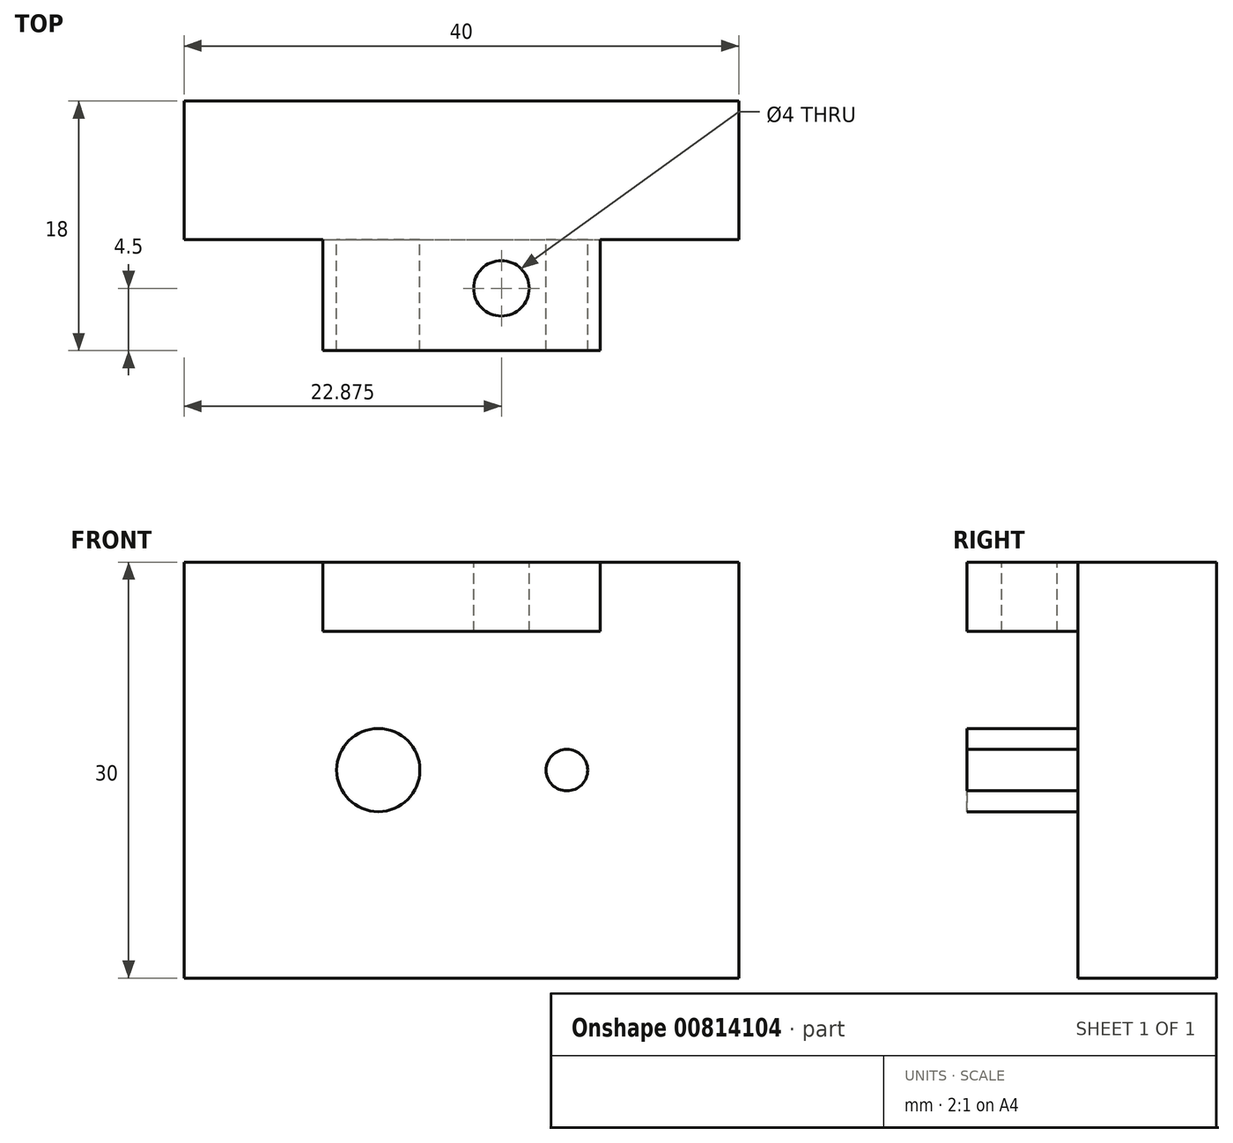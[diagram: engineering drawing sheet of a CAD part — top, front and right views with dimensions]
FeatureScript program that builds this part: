
annotation { "Feature Type Name" : "Feature", "Feature Type Description" : "" }
export const myFeature = defineFeature(function(context is Context, id is Id, definition is map)
    precondition{}
    {
        {
            var Q0;
            Q0=qCreatedBy(makeId("Front.planeOp"),FACE);
            var sketch = newSketch(context, id + "F0", { "sketchPlane" : qUnion([Q0])});
            skLineSegment(sketch, "E0.bottom", {"start": v(0, 0) * mm, "end": v(40, 0) * mm});
            skLineSegment(sketch, "E0.top", {"start": v(0, 30) * mm, "end": v(40, 30) * mm});
            skLineSegment(sketch, "E0.left", {"start": v(0, 0) * mm, "end": v(0, 30) * mm});
            skLineSegment(sketch, "E0.right", {"start": v(40, 0) * mm, "end": v(40, 30) * mm});
            skSolve(sketch);
        }
        {
            var Q0;
            Q0 = qSketchRegion(id + "F0", true);
            extrude(context, id + "F1", {"entities" : qUnion([Q0]), "depth" : 10 * mm, "offsetDistance" : 25 * mm});
        }
        {
            var Q0;
            Q0=makeQuery(id+"F1.opExtrude","CAP_FACE",FACE,{"disambiguationData":[OSD([sQuery(id+"F0.wireOp",EDGE,"E0.bottom"),sQuery(id+"F0.wireOp",EDGE,"E0.top"),sQuery(id+"F0.wireOp",EDGE,"E0.left"),sQuery(id+"F0.wireOp",EDGE,"E0.right")])],"isStart":false});
            var sketch = newSketch(context, id + "F2", { "sketchPlane" : qUnion([Q0])});
            skCircle(sketch, "E1", {"center": v(14, 15) * mm, "radius": 3 * mm});
            skPoint(sketch, "E1.centerSnap0", {"position": v(0, 15) * mm});
            skCircle(sketch, "E2", {"center": v(27.6, 15) * mm, "radius": 1.5 * mm});
            skLineSegment(sketch, "E3.bottom", {"start": v(10, 30) * mm, "end": v(30, 30) * mm});
            skLineSegment(sketch, "E3.top", {"start": v(10, 25) * mm, "end": v(30, 25) * mm});
            skLineSegment(sketch, "E3.left", {"start": v(10, 30) * mm, "end": v(10, 25) * mm});
            skLineSegment(sketch, "E3.right", {"start": v(30, 30) * mm, "end": v(30, 25) * mm});
            skSolve(sketch);
        }
        {
            var Q0;
            Q0 = qSketchRegion(id + "F2", true);
            extrude(context, id + "F3", {"entities" : qUnion([Q0]), "operationType" : NewBodyOperationType.ADD, "depth" : 8 * mm, "offsetDistance" : 25 * mm});
        }
        {
            var Q0;
            Q0=makeQuery(id+"F3.boolean.opBoolean","MERGE",FACE,{"derivedFrom":[makeQuery(id+"F1.opExtrude","SWEPT_FACE",FACE,{"disambiguationData":[OSD([sQuery(id+"F0.wireOp",EDGE,"E0.top")])]}),makeQuery(id+"F3.opExtrude","SWEPT_FACE",FACE,{"disambiguationData":[OSD([sQuery(id+"F2.wireOp",EDGE,"E3.bottom")])]})]});
            var sketch = newSketch(context, id + "F4", { "sketchPlane" : qUnion([Q0])});
            skCircle(sketch, "E4", {"center": v(22.88, -13.5) * mm, "radius": 2 * mm});
            skSolve(sketch);
        }
        {
            var Q0;
            Q0 = qSketchRegion(id + "F4", true);
            extrude(context, id + "F5", {"entities" : qUnion([Q0]), "operationType" : NewBodyOperationType.REMOVE, "endBound" : BoundingType.UP_TO_NEXT, "oppositeDirection" : true, "depth" : 25 * mm, "offsetDistance" : 25 * mm});
        }
    });
